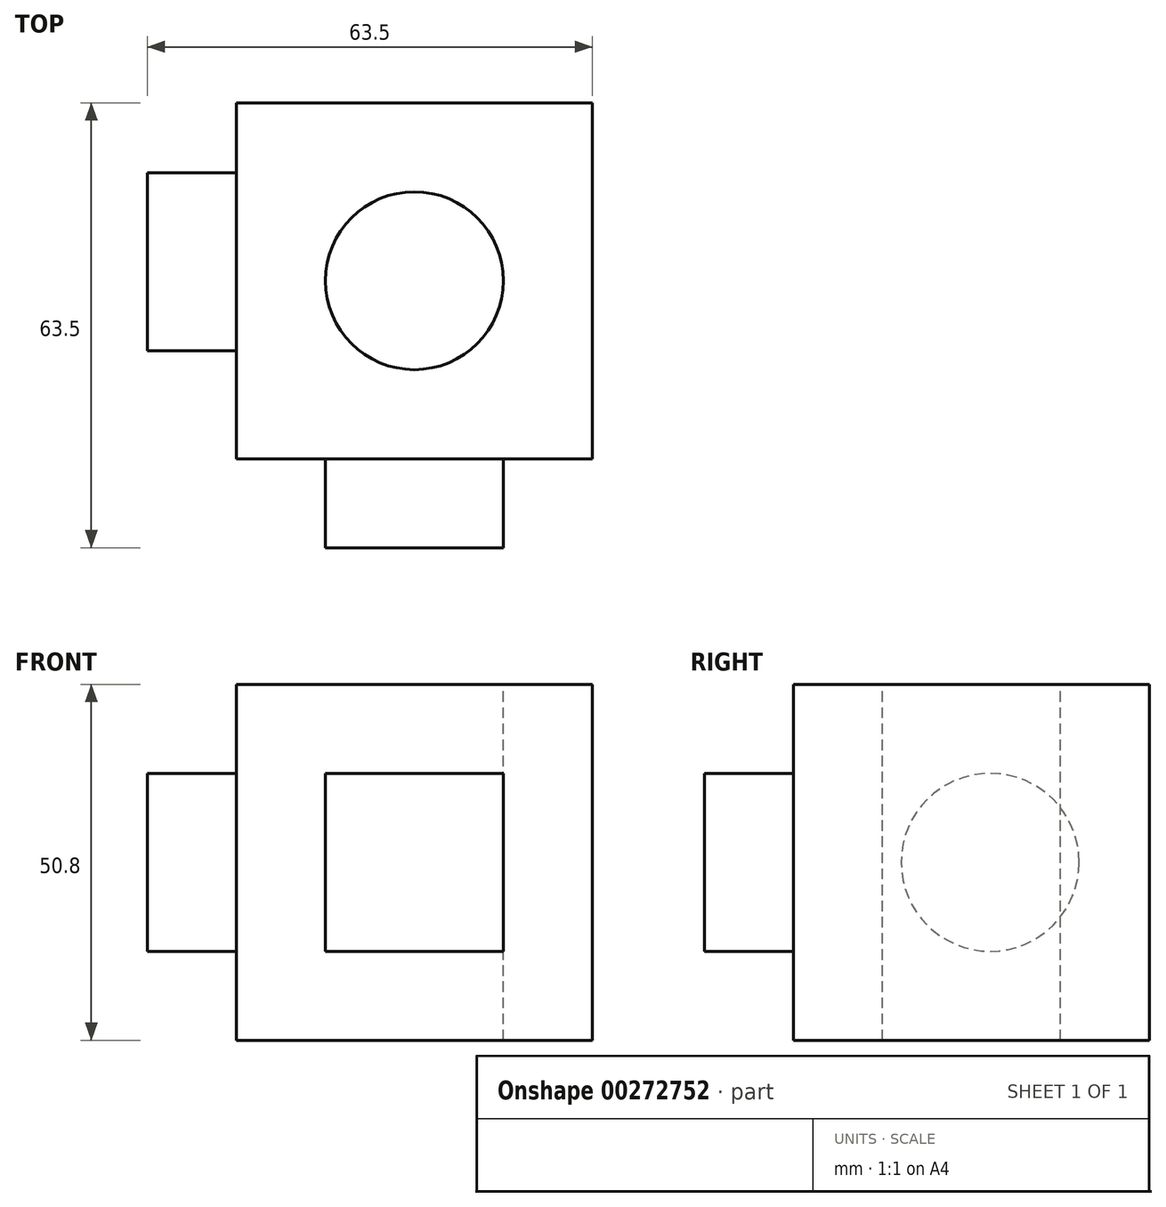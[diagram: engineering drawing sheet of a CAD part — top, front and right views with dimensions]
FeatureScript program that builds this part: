
annotation { "Feature Type Name" : "Feature", "Feature Type Description" : "" }
export const myFeature = defineFeature(function(context is Context, id is Id, definition is map)
    precondition{}
    {
        {
            var Q0;
            Q0=qCreatedBy(makeId("Front.planeOp"),FACE);
            var sketch = newSketch(context, id + "F0", { "sketchPlane" : qUnion([Q0])});
            skLineSegment(sketch, "E0.bottom", {"start": v(0, 0) * mm, "end": v(-50.8, 0) * mm});
            skLineSegment(sketch, "E0.top", {"start": v(0, 50.8) * mm, "end": v(-50.8, 50.8) * mm});
            skLineSegment(sketch, "E0.left", {"start": v(0, 0) * mm, "end": v(0, 50.8) * mm});
            skLineSegment(sketch, "E0.right", {"start": v(-50.8, 0) * mm, "end": v(-50.8, 50.8) * mm});
            skSolve(sketch);
        }
        {
            var Q0;
            Q0 = qSketchRegion(id + "F0", true);
            extrude(context, id + "F1", {"entities" : qUnion([Q0]), "depth" : 50.8 * mm});
        }
        {
            var Q0;
            Q0=makeQuery(id+"F1.opExtrude","CAP_FACE",FACE,{"disambiguationData":[OSD([sQuery(id+"F0.wireOp",EDGE,"E0.bottom"),sQuery(id+"F0.wireOp",EDGE,"E0.top"),sQuery(id+"F0.wireOp",EDGE,"E0.left"),sQuery(id+"F0.wireOp",EDGE,"E0.right")])],"isStart":false});
            var sketch = newSketch(context, id + "F2", { "sketchPlane" : qUnion([Q0])});
            skLineSegment(sketch, "E1.bottom", {"start": v(-38.1, 38.1) * mm, "end": v(-12.7, 38.1) * mm});
            skLineSegment(sketch, "E1.top", {"start": v(-38.1, 12.7) * mm, "end": v(-12.7, 12.7) * mm});
            skLineSegment(sketch, "E1.left", {"start": v(-38.1, 38.1) * mm, "end": v(-38.1, 12.7) * mm});
            skLineSegment(sketch, "E1.right", {"start": v(-12.7, 38.1) * mm, "end": v(-12.7, 12.7) * mm});
            skSolve(sketch);
        }
        {
            var Q0;
            Q0=makeQuery(id+"F2.imprint","IMPRINT",FACE,{"disambiguationData":[TD([[makeQuery(id+"F2.imprint","IMPRINT",EDGE,{"derivedFrom":sQuery(id+"F2.wireOp",EDGE,"E1.bottom")}),-1.0]])]});
            extrude(context, id + "F3", {"entities" : qUnion([Q0]), "operationType" : NewBodyOperationType.ADD, "depth" : 12.7 * mm});
        }
        {
            var Q0;
            Q0=makeQuery(id+"F1.opExtrude","SWEPT_FACE",FACE,{"disambiguationData":[OSD([sQuery(id+"F0.wireOp",EDGE,"E0.top")])]});
            var sketch = newSketch(context, id + "F4", { "sketchPlane" : qUnion([Q0])});
            skCircle(sketch, "E2", {"center": v(-25.4, -25.4) * mm, "radius": 12.7 * mm});
            skSolve(sketch);
        }
        {
            var Q0;
            Q0=makeQuery(id+"F4.imprint","IMPRINT",FACE,{"disambiguationData":[TD([[makeQuery(id+"F4.imprint","IMPRINT",EDGE,{"derivedFrom":sQuery(id+"F4.wireOp",EDGE,"E2")}),1.0]])]});
            extrude(context, id + "F5", {"entities" : qUnion([Q0]), "operationType" : NewBodyOperationType.REMOVE, "oppositeDirection" : true, "depth" : 50.8 * mm});
        }
        {
            var Q0;
            Q0=makeQuery(id+"F1.opExtrude","SWEPT_FACE",FACE,{"disambiguationData":[OSD([sQuery(id+"F0.wireOp",EDGE,"E0.right")])]});
            var sketch = newSketch(context, id + "F6", { "sketchPlane" : qUnion([Q0])});
            skCircle(sketch, "E3", {"center": v(22.72, 25.4) * mm, "radius": 12.7 * mm});
            skSolve(sketch);
        }
        {
            var Q0;
            Q0=makeQuery(id+"F6.imprint","IMPRINT",FACE,{"disambiguationData":[TD([[makeQuery(id+"F6.imprint","IMPRINT",EDGE,{"derivedFrom":sQuery(id+"F6.wireOp",EDGE,"E3")}),1.0]])]});
            extrude(context, id + "F7", {"entities" : qUnion([Q0]), "operationType" : NewBodyOperationType.ADD, "depth" : 12.7 * mm});
        }
    });
